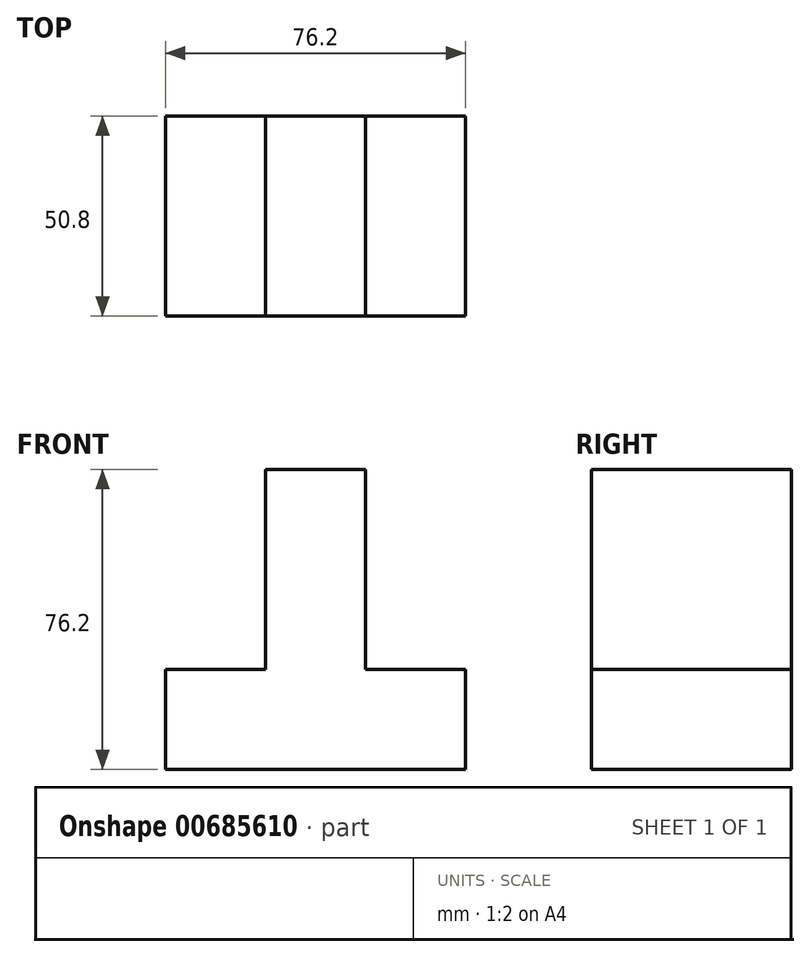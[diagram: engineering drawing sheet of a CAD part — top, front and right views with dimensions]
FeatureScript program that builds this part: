
annotation { "Feature Type Name" : "Feature", "Feature Type Description" : "" }
export const myFeature = defineFeature(function(context is Context, id is Id, definition is map)
    precondition{}
    {
        {
            var Q0;
            Q0=qCreatedBy(makeId("Front.planeOp"),FACE);
            var sketch = newSketch(context, id + "F0", { "sketchPlane" : qUnion([Q0])});
            skLineSegment(sketch, "E0", {"start": v(-41.15, 0) * mm, "end": v(35.05, 0) * mm});
            skLineSegment(sketch, "E1", {"start": v(35.05, 0) * mm, "end": v(35.05, 25.4) * mm});
            skLineSegment(sketch, "E2", {"start": v(35.05, 25.4) * mm, "end": v(9.65, 25.4) * mm});
            skLineSegment(sketch, "E3", {"start": v(9.65, 25.4) * mm, "end": v(9.65, 76.2) * mm});
            skLineSegment(sketch, "E4", {"start": v(9.65, 76.2) * mm, "end": v(-15.75, 76.2) * mm});
            skLineSegment(sketch, "E5", {"start": v(-15.75, 76.2) * mm, "end": v(-15.75, 25.4) * mm});
            skLineSegment(sketch, "E6", {"start": v(-15.75, 25.4) * mm, "end": v(-41.15, 25.4) * mm});
            skLineSegment(sketch, "E7", {"start": v(-41.15, 25.4) * mm, "end": v(-41.15, 0) * mm});
            skSolve(sketch);
        }
        {
            var Q0;
            Q0 = qSketchRegion(id + "F0", true);
            extrude(context, id + "F1", {"entities" : qUnion([Q0]), "depth" : 50.8 * mm, "offsetDistance" : 25.4 * mm});
        }
    });
